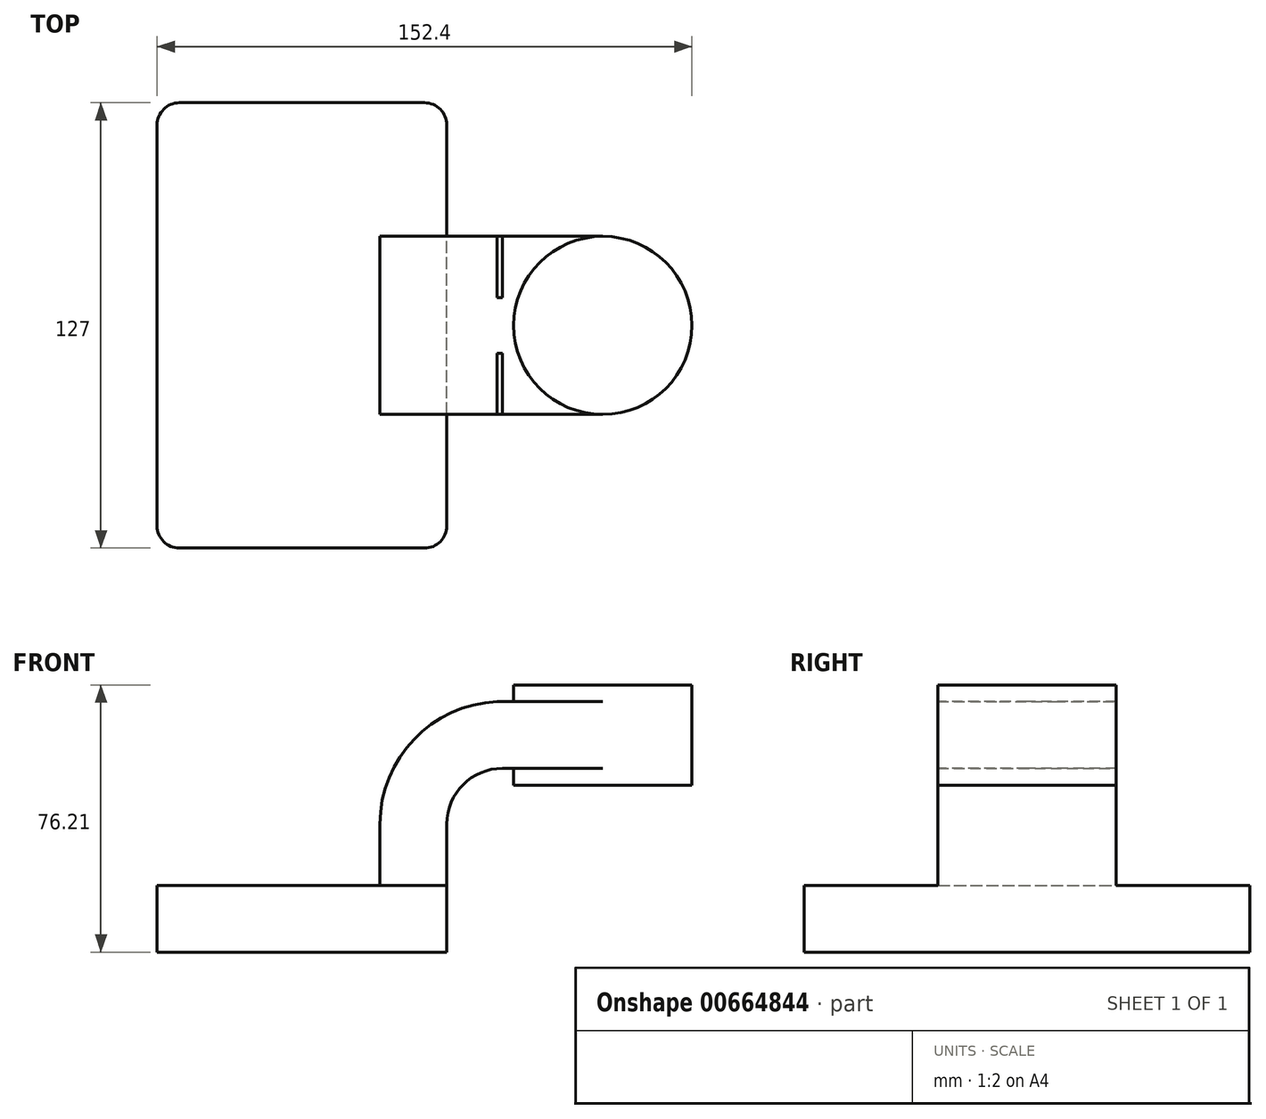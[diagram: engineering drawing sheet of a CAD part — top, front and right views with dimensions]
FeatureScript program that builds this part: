
annotation { "Feature Type Name" : "Feature", "Feature Type Description" : "" }
export const myFeature = defineFeature(function(context is Context, id is Id, definition is map)
    precondition{}
    {
        {
            var Q0;
            Q0=qCreatedBy(makeId("Front.planeOp"),FACE);
            var sketch = newSketch(context, id + "F0", { "sketchPlane" : qUnion([Q0])});
            skLineSegment(sketch, "E0.bottom", {"start": v(-41.28, 9.53) * mm, "end": v(41.28, 9.53) * mm});
            skLineSegment(sketch, "E0.top", {"start": v(-41.28, -9.53) * mm, "end": v(41.28, -9.53) * mm});
            skLineSegment(sketch, "E0.left", {"start": v(-41.28, 9.53) * mm, "end": v(-41.28, -9.53) * mm});
            skLineSegment(sketch, "E0.right", {"start": v(41.28, 9.53) * mm, "end": v(41.28, -9.53) * mm});
            skPoint(sketch, "E0.middle", {"position": v(0, 0) * mm});
            skLineSegment(sketch, "E1.bottom", {"start": v(60.32, 66.67) * mm, "end": v(111.12, 66.67) * mm});
            skLineSegment(sketch, "E1.top", {"start": v(60.32, 38.1) * mm, "end": v(111.12, 38.1) * mm});
            skLineSegment(sketch, "E1.left", {"start": v(60.32, 66.67) * mm, "end": v(60.32, 38.1) * mm});
            skLineSegment(sketch, "E1.right", {"start": v(111.12, 66.68) * mm, "end": v(111.12, 38.1) * mm});
            skPoint(sketch, "E1.middle", {"position": v(85.72, 52.39) * mm});
            skPoint(sketch, "E2.endSnap0", {"position": v(85.72, 38.1) * mm});
            skLineSegment(sketch, "E3", {"start": v(41.28, 9.53) * mm, "end": v(41.28, 27) * mm});
            skArc(sketch, "E4", {"start": v(41.28, 27) * mm, "mid": v(45.92, 38.23) * mm, "end": v(57.15, 42.88) * mm});
            skLineSegment(sketch, "E5", {"start": v(57.15, 42.88) * mm, "end": v(85.72, 42.88) * mm});
            skLineSegment(sketch, "E6.0", {"start": v(57.15, 61.93) * mm, "end": v(85.72, 61.93) * mm});
            skArc(sketch, "E6.1", {"start": v(22.23, 27) * mm, "mid": v(32.45, 51.7) * mm, "end": v(57.15, 61.93) * mm});
            skLineSegment(sketch, "E6.2", {"start": v(22.23, 9.53) * mm, "end": v(22.23, 27) * mm});
            skLineSegment(sketch, "E7", {"start": v(85.72, 42.88) * mm, "end": v(85.72, 61.93) * mm});
            skFitSpline(sketch, "E8", {"points": [v(-41.28, 9.53) * mm, v(57.15, 61.93) * mm], "startDerivative": vector(0.18, 125.64) * mm, "endDerivative": vector(121.32, 2.32) * mm});
            skLineSegment(sketch, "E9", {"start": v(85.72, 61.93) * mm, "end": v(85.72, 66.67) * mm});
            skLineSegment(sketch, "E10", {"start": v(85.72, 42.88) * mm, "end": v(85.72, 38.1) * mm});
            skSolve(sketch);
        }
        {
            var Q0;
            Q0=makeQuery(id+"F0.imprint","IMPRINT",FACE,{"disambiguationData":[TD([[makeQuery(id+"F0.imprint","IMPRINT",EDGE,{"derivedFrom":sQuery(id+"F0.wireOp",EDGE,"E0.top")}),1.0]])]});
            extrude(context, id + "F1", {"entities" : qUnion([Q0]), "endBound" : BoundingType.SYMMETRIC, "depth" : 127 * mm, "offsetDistance" : 25.4 * mm});
        }
        {
            var Q0;
            Q0 = qSketchRegion(id + "FFkVkmpO1EB4bGF_0", true);
            var Q1;
            {var subQ1=sQuery(id+"F0.wireOp",EDGE,"E3");Q1=makeQuery(id+"F0.imprint","IMPRINT",FACE,{"disambiguationData":[TD([[makeQuery(id+"F0.imprint","IMPRINT",EDGE,{"derivedFrom":subQ1}),1.0]])]});}
            var Q2;
            {var subQ5=sQuery(id+"F0.wireOp",EDGE,"E7");Q2=makeQuery(id+"F0.imprint","IMPRINT",FACE,{"disambiguationData":[TD([[makeQuery(id+"F0.imprint","IMPRINT",EDGE,{"derivedFrom":subQ5}),1.0]])]});}
            extrude(context, id + "F2", {"entities" : qUnion([Q0, Q1, Q2]), "operationType" : NewBodyOperationType.ADD, "endBound" : BoundingType.SYMMETRIC, "depth" : 50.8 * mm, "offsetDistance" : 25.4 * mm});
        }
        {
            var Q0;
            Q0=makeQuery(id+"F0.imprint","IMPRINT",FACE,{"disambiguationData":[TD([[makeQuery(id+"F0.imprint","IMPRINT",EDGE,{"derivedFrom":sQuery(id+"F0.wireOp",EDGE,"E6.1")}),1.0]])]});
            extrude(context, id + "F3", {"entities" : qUnion([Q0]), "operationType" : NewBodyOperationType.ADD, "endBound" : BoundingType.SYMMETRIC, "depth" : 15.88 * mm, "offsetDistance" : 25.4 * mm});
        }
        {
            var Q0;
            {var subQ0=sQuery(id+"F0.wireOp",EDGE,"E1.right");Q0=makeQuery(id+"F0.imprint","IMPRINT",FACE,{"disambiguationData":[TD([[makeQuery(id+"F0.imprint","IMPRINT",EDGE,{"derivedFrom":subQ0}),-1.0]])]});}
            var Q1;
            Q1=sQuery(id+"F0.wireOp",EDGE,"E7");
            revolve(context, id + "F4", {"operationType" : NewBodyOperationType.ADD, "entities" : qUnion([Q0]), "axis" : qUnion([Q1]), "revolveType" : RevolveType.FULL});
        }
        {
            var Q0;
            Q0=makeQuery(id+"F1.opExtrude","CAP_EDGE",EDGE,{"disambiguationData":[OSD([sQuery(id+"F0.wireOp",EDGE,"E0.left")])],"isStart":true});
            fillet(context, id + "F5", {"entities" : qUnion([Q0]), "radius" : 6.35 * mm, "tangentPropagation" : true, "allowEdgeOverflow" : false});
        }
        {
            var Q0;
            Q0=makeQuery(id+"F1.opExtrude","CAP_EDGE",EDGE,{"disambiguationData":[OSD([sQuery(id+"F0.wireOp",EDGE,"E0.left")])],"isStart":false});
            var Q1;
            Q1=makeQuery(id+"F1.opExtrude","CAP_EDGE",EDGE,{"disambiguationData":[OSD([sQuery(id+"F0.wireOp",EDGE,"E0.right")])],"isStart":true});
            var Q2;
            Q2=makeQuery(id+"F1.opExtrude","CAP_EDGE",EDGE,{"disambiguationData":[OSD([sQuery(id+"F0.wireOp",EDGE,"E0.right")])],"isStart":false});
            fillet(context, id + "F6", {"entities" : qUnion([Q0, Q1, Q2]), "radius" : 6.35 * mm, "tangentPropagation" : true, "allowEdgeOverflow" : false});
        }
    });
